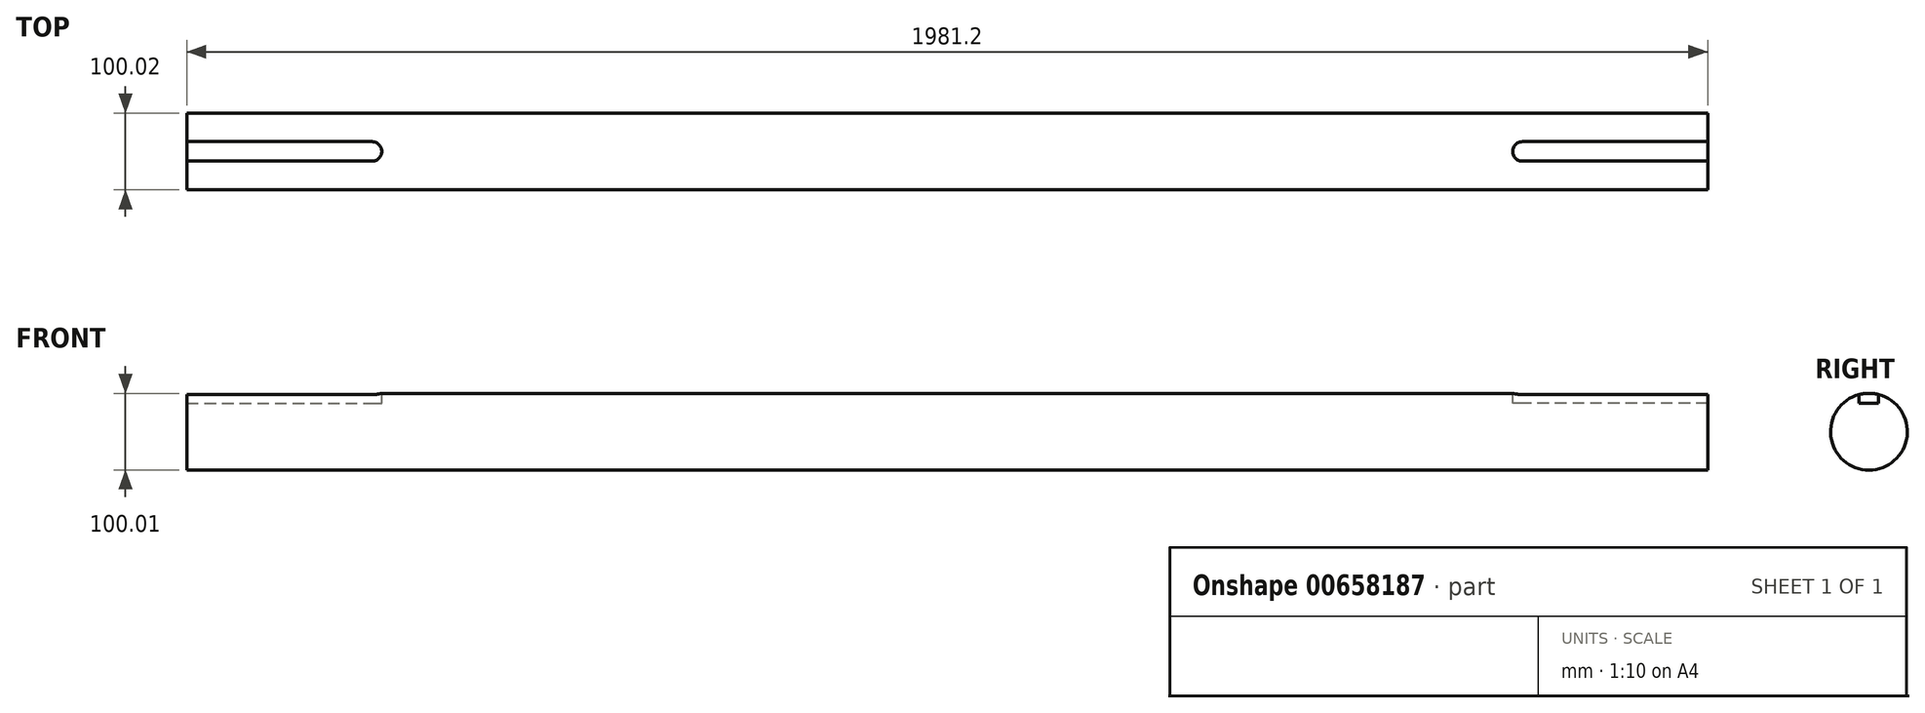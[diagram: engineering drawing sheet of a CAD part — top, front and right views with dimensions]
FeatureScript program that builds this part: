
annotation { "Feature Type Name" : "Feature", "Feature Type Description" : "" }
export const myFeature = defineFeature(function(context is Context, id is Id, definition is map)
    precondition{}
    {
        {
            var Q0;
            Q0=qCreatedBy(makeId("Right.planeOp"),FACE);
            var sketch = newSketch(context, id + "F0", { "sketchPlane" : qUnion([Q0])});
            skCircle(sketch, "E0", {"center": v(0, -50) * mm, "radius": 50 * mm});
            skSolve(sketch);
        }
        {
            var Q0;
            Q0 = qSketchRegion(id + "F0", true);
            extrude(context, id + "F1", {"entities" : qUnion([Q0]), "endBound" : BoundingType.SYMMETRIC, "depth" : 1981.2 * mm, "offsetDistance" : 25.4 * mm});
        }
        {
            var Q0;
            Q0=qCreatedBy(makeId("Top.planeOp"),FACE);
            var sketch = newSketch(context, id + "F2", { "sketchPlane" : qUnion([Q0])});
            skLineSegment(sketch, "E1", {"start": v(-495.3, 50) * mm, "end": v(495.3, 50) * mm});
            skLineSegment(sketch, "E2", {"start": v(495.3, -50) * mm, "end": v(-495.3, -50) * mm});
            skLineSegment(sketch, "E3.0", {"start": v(990.6, 50) * mm, "end": v(990.6, -50) * mm});
            skLineSegment(sketch, "E4.0", {"start": v(-990.6, 50) * mm, "end": v(-990.6, -50) * mm});
            skLineSegment(sketch, "E5.bottom", {"start": v(-990.6, -12.7) * mm, "end": v(-749.3, -12.7) * mm});
            skLineSegment(sketch, "E5.top", {"start": v(-990.6, 12.7) * mm, "end": v(-749.3, 12.7) * mm});
            skLineSegment(sketch, "E5.left", {"start": v(-990.6, -12.7) * mm, "end": v(-990.6, 12.7) * mm});
            skLineSegment(sketch, "E5.right", {"start": v(-736.6, 0) * mm, "end": v(-736.6, 0) * mm});
            skPoint(sketch, "E5.middle", {"position": v(-863.6, 0) * mm});
            skLineSegment(sketch, "E6.MirrorCS", {"start": v(990.6, 12.7) * mm, "end": v(749.3, 12.7) * mm});
            skLineSegment(sketch, "E7.MirrorCS", {"start": v(736.6, 0) * mm, "end": v(736.6, 0) * mm});
            skLineSegment(sketch, "E8.MirrorCS", {"start": v(990.6, -12.7) * mm, "end": v(749.3, -12.7) * mm});
            skPoint(sketch, "E9.visualSharp", {"position": v(736.6, 12.7) * mm});
            skArc(sketch, "E9.filletArc", {"start": v(749.3, 12.7) * mm, "mid": v(740.32, 8.98) * mm, "end": v(736.6, 0) * mm});
            skPoint(sketch, "E10.visualSharp", {"position": v(736.6, -12.7) * mm});
            skArc(sketch, "E10.filletArc", {"start": v(736.6, 0) * mm, "mid": v(740.32, -8.98) * mm, "end": v(749.3, -12.7) * mm});
            skPoint(sketch, "E11.visualSharp", {"position": v(-736.6, 12.7) * mm});
            skArc(sketch, "E11.filletArc", {"start": v(-736.6, 0) * mm, "mid": v(-740.32, 8.98) * mm, "end": v(-749.3, 12.7) * mm});
            skPoint(sketch, "E12.visualSharp", {"position": v(-736.6, -12.7) * mm});
            skArc(sketch, "E12.filletArc", {"start": v(-749.3, -12.7) * mm, "mid": v(-740.32, -8.98) * mm, "end": v(-736.6, 0) * mm});
            skSolve(sketch);
        }
        {
            var Q0;
            Q0=makeQuery(id+"F2.imprint","IMPRINT",FACE,{"disambiguationData":[TD([[makeQuery(id+"F2.imprint","IMPRINT",EDGE,{"derivedFrom":sQuery(id+"F2.wireOp",EDGE,"E5.bottom")}),1.0]])]});
            var Q1;
            {var subQ1=sQuery(id+"F2.wireOp",EDGE,"E6.MirrorCS");Q1=makeQuery(id+"F2.imprint","IMPRINT",FACE,{"disambiguationData":[TD([[makeQuery(id+"F2.imprint","IMPRINT",EDGE,{"derivedFrom":subQ1}),1.0]])]});}
            extrude(context, id + "F3", {"entities" : qUnion([Q0, Q1]), "operationType" : NewBodyOperationType.REMOVE, "oppositeDirection" : true, "depth" : 12.73 * mm, "offsetDistance" : 25.4 * mm});
        }
    });
